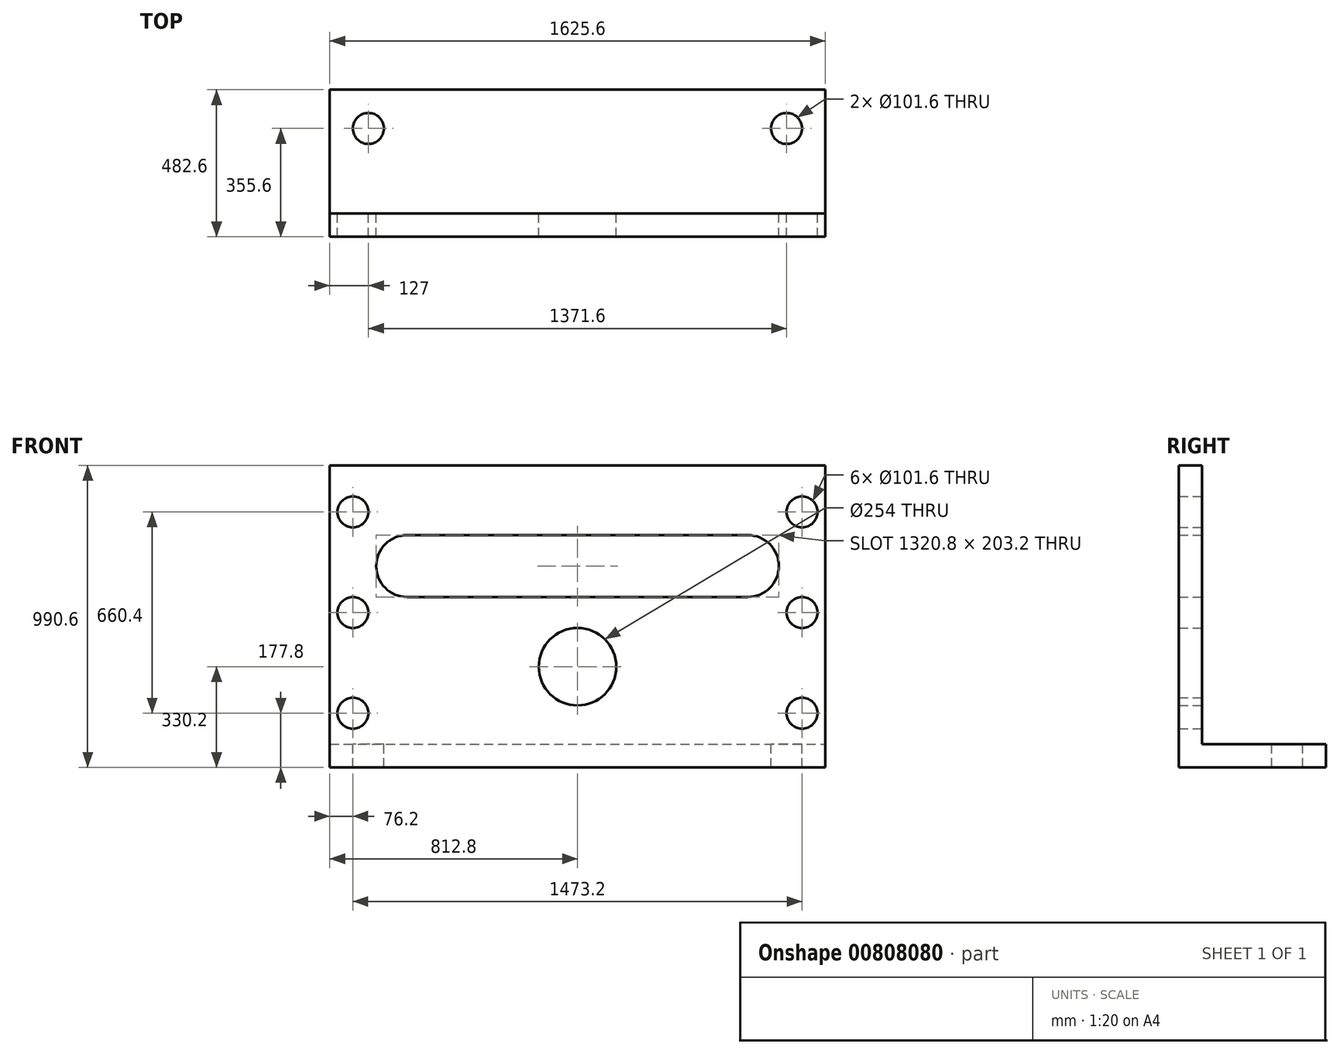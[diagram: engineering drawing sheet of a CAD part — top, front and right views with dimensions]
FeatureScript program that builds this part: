
annotation { "Feature Type Name" : "Feature", "Feature Type Description" : "" }
export const myFeature = defineFeature(function(context is Context, id is Id, definition is map)
    precondition{}
    {
        {
            var Q0;
            Q0=qCreatedBy(makeId("Top.planeOp"),FACE);
            var sketch = newSketch(context, id + "F0", { "sketchPlane" : qUnion([Q0])});
            skLineSegment(sketch, "E0.bottom", {"start": v(812.8, -241.3) * mm, "end": v(-812.8, -241.3) * mm});
            skLineSegment(sketch, "E0.top", {"start": v(812.8, 241.3) * mm, "end": v(-812.8, 241.3) * mm});
            skLineSegment(sketch, "E0.left", {"start": v(812.8, -241.3) * mm, "end": v(812.8, 241.3) * mm});
            skLineSegment(sketch, "E0.right", {"start": v(-812.8, -241.3) * mm, "end": v(-812.8, 241.3) * mm});
            skPoint(sketch, "E0.middle", {"position": v(0, 0) * mm});
            skSolve(sketch);
        }
        {
            var Q0;
            Q0 = qSketchRegion(id + "F0", true);
            extrude(context, id + "F1", {"entities" : qUnion([Q0]), "depth" : 76.2 * mm, "offsetDistance" : 25.4 * mm});
        }
        {
            var Q0;
            Q0=makeQuery(id+"F1.opExtrude","CAP_FACE",FACE,{"disambiguationData":[OSD([sQuery(id+"F0.wireOp",EDGE,"E0.bottom"),sQuery(id+"F0.wireOp",EDGE,"E0.top"),sQuery(id+"F0.wireOp",EDGE,"E0.left"),sQuery(id+"F0.wireOp",EDGE,"E0.right")])],"isStart":false});
            var sketch = newSketch(context, id + "F2", { "sketchPlane" : qUnion([Q0])});
            skLineSegment(sketch, "E1.bottom", {"start": v(-812.8, -241.3) * mm, "end": v(812.8, -241.3) * mm});
            skLineSegment(sketch, "E1.top", {"start": v(-812.8, -165.1) * mm, "end": v(812.8, -165.1) * mm});
            skLineSegment(sketch, "E1.left", {"start": v(-812.8, -241.3) * mm, "end": v(-812.8, -165.1) * mm});
            skLineSegment(sketch, "E1.right", {"start": v(812.8, -241.3) * mm, "end": v(812.8, -165.1) * mm});
            skSolve(sketch);
        }
        {
            var Q0;
            Q0 = qSketchRegion(id + "F2", true);
            extrude(context, id + "F3", {"entities" : qUnion([Q0]), "operationType" : NewBodyOperationType.ADD, "depth" : 914.4 * mm, "offsetDistance" : 25.4 * mm});
        }
        {
            var Q0;
            Q0=makeQuery(id+"F3.opExtrude","SWEPT_FACE",FACE,{"disambiguationData":[OSD([sQuery(id+"F2.wireOp",EDGE,"E1.top")])]});
            var sketch = newSketch(context, id + "F4", { "sketchPlane" : qUnion([Q0])});
            skLineSegment(sketch, "E2", {"start": v(0, 0) * mm, "end": v(0, 330.2) * mm});
            skCircle(sketch, "E3", {"center": v(0, 330.2) * mm, "radius": 127 * mm});
            skLineSegment(sketch, "E4", {"start": v(0, 330.2) * mm, "end": v(-558.8, 330.2) * mm});
            skArc(sketch, "E5", {"start": v(-558.8, 762) * mm, "mid": v(-660.4, 660.4) * mm, "end": v(-558.8, 558.8) * mm});
            skArc(sketch, "E6", {"start": v(558.8, 558.8) * mm, "mid": v(660.4, 660.4) * mm, "end": v(558.8, 762) * mm});
            skLineSegment(sketch, "E7", {"start": v(-558.8, 762) * mm, "end": v(558.8, 762) * mm});
            skLineSegment(sketch, "E8", {"start": v(-558.8, 558.8) * mm, "end": v(558.8, 558.8) * mm});
            skPoint(sketch, "E9.orphan", {"position": v(0, 660.4) * mm});
            skSolve(sketch);
        }
        {
            var Q0;
            Q0 = qSketchRegion(id + "F4", true);
            extrude(context, id + "F5", {"entities" : qUnion([Q0]), "operationType" : NewBodyOperationType.REMOVE, "oppositeDirection" : true, "depth" : 612.14 * mm, "offsetDistance" : 25.4 * mm});
        }
        {
            var Q0;
            Q0=makeQuery(id+"F3.opExtrude","SWEPT_FACE",FACE,{"disambiguationData":[OSD([sQuery(id+"F2.wireOp",EDGE,"E1.top")])]});
            var sketch = newSketch(context, id + "F6", { "sketchPlane" : qUnion([Q0])});
            skLineSegment(sketch, "E10", {"start": v(812.8, 990.6) * mm, "end": v(812.8, 838.2) * mm});
            skLineSegment(sketch, "E11", {"start": v(812.8, 838.2) * mm, "end": v(736.6, 838.2) * mm});
            skLineSegment(sketch, "E12", {"start": v(736.6, 838.2) * mm, "end": v(736.6, 508) * mm});
            skLineSegment(sketch, "E13", {"start": v(736.6, 508) * mm, "end": v(736.6, 177.8) * mm});
            skCircle(sketch, "E14", {"center": v(736.6, 838.2) * mm, "radius": 50.8 * mm});
            skCircle(sketch, "E15", {"center": v(736.6, 508) * mm, "radius": 50.8 * mm});
            skCircle(sketch, "E16", {"center": v(736.6, 177.8) * mm, "radius": 50.8 * mm});
            skLineSegment(sketch, "E17", {"start": v(-812.8, 990.6) * mm, "end": v(-736.6, 990.6) * mm});
            skLineSegment(sketch, "E18", {"start": v(-736.6, 990.6) * mm, "end": v(-736.6, 838.2) * mm});
            skLineSegment(sketch, "E19", {"start": v(-736.6, 838.2) * mm, "end": v(-736.6, 508) * mm});
            skLineSegment(sketch, "E20", {"start": v(-736.6, 508) * mm, "end": v(-736.6, 177.8) * mm});
            skCircle(sketch, "E21", {"center": v(-736.6, 838.2) * mm, "radius": 50.8 * mm});
            skCircle(sketch, "E22", {"center": v(-736.6, 508) * mm, "radius": 50.8 * mm});
            skCircle(sketch, "E23", {"center": v(-736.6, 177.8) * mm, "radius": 50.8 * mm});
            skSolve(sketch);
        }
        {
            var Q0;
            Q0 = qSketchRegion(id + "F6", true);
            extrude(context, id + "F7", {"entities" : qUnion([Q0]), "operationType" : NewBodyOperationType.REMOVE, "oppositeDirection" : true, "depth" : 281.94 * mm, "offsetDistance" : 25.4 * mm});
        }
        {
            var Q0;
            Q0=makeQuery(id+"F1.opExtrude","CAP_FACE",FACE,{"disambiguationData":[OSD([sQuery(id+"F0.wireOp",EDGE,"E0.bottom"),sQuery(id+"F0.wireOp",EDGE,"E0.top"),sQuery(id+"F0.wireOp",EDGE,"E0.left"),sQuery(id+"F0.wireOp",EDGE,"E0.right")])],"isStart":false});
            var sketch = newSketch(context, id + "F8", { "sketchPlane" : qUnion([Q0])});
            skCircle(sketch, "E24", {"center": v(-685.8, 114.3) * mm, "radius": 50.8 * mm});
            skCircle(sketch, "E25", {"center": v(685.8, 114.3) * mm, "radius": 50.8 * mm});
            skSolve(sketch);
        }
        {
            var Q0;
            Q0 = qSketchRegion(id + "F8", true);
            extrude(context, id + "F9", {"entities" : qUnion([Q0]), "operationType" : NewBodyOperationType.REMOVE, "oppositeDirection" : true, "depth" : 215.9 * mm, "offsetDistance" : 25.4 * mm});
        }
    });
